# Revit family: FA-SERIES
name_source: partatom
category: Generic Models
revit_build: Autodesk Revit LT 2016 (Build: 20161004_0715(x64)
units: mm (PartAtom-declared; Revit-internal decimal feet)

## family parameters
Always vertical = Yes
Can host rebar = No
Cut with Voids When Loaded = No
Part Type = Normal
Room Calculation Point = No
Round Connector Dimension = Use Diameter
Shared = No
Work Plane-Based = No

## types (5) — shared parameters
Manufacturer = REVERSOMATIC
Submittals = http://www.reversomatic.com
URL = http://www.reversomatic.com

## per-type parameters (varying)
| type | A | B | BB | C | D | E | F | G | H | J |
| FA 18 | 45.31 " | -40.25 " | -40 " | -20.75 " | 36.38 " | 18.88 " | 21.88 " | 7.25 " | 11 " | 6.5 " |
| FA 15 | 42.62 " | -33.12 " | -32.87 " | -16.5 " | 32.38 " | 15.88 " | 18.62 " | 6.88 " | 10.25 " | 6.25 " |
| FA 12 | 42.62 " | -33.12 " | -32.87 " | -16.5 " | 32.38 " | 13.44 " | 15.62 " | 8.36 " | 9.47 " | 9.47 " |
| FA 10 | 38.5 " | -30 " | -29.75 " | -12.25 " | 28.38 " | 11.38 " | 13.12 " | 7.62 " | 8.5 " | 8.5 " |
| FA 9 | 32.38 " | -26.12 " | -25.87 " | -10.25 " | 24.35 " | 10.25 " | 11.81 " | 6.28 " | 7.06 " | 7.06 " |

note: column(s) folded — value = type name in every type: Model

## geometry (parser evidence)
native form markers: Sweep x3
no freeform markers — native parametric forms only
